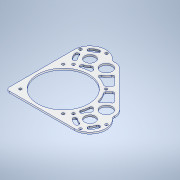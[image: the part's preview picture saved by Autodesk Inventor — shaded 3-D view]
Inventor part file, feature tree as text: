
AUTODESK INVENTOR PART (.ipt)
format: ipt  version: 2020 (Build 240168000, 168)  size: 512,512 bytes
history: native  units: in
note: dims shown in document units (in); Inventor stores cm internally (conversion verified against a paired STEP export)
features: extrude x4, sketch x3, fillet x1
ambient origin geometry x8: Origin, YZ Plane, XZ Plane, XY Plane, X Axis, Y Axis, Z Axis, Center Point
bodies: Solid1 (feature_tree)
feature tree (8):
  extrude  "Extrusion1"  Depth=4.5in
  extrude  "Extrusion2"  Depth=4.25in
  extrude  "Extrusion5"  Depth=0.25in
  fillet  "Fillet3"  Radius=5.9094in
  extrude  "Extrusion6"  Depth=0.25in
  sketch  "Sketch1"  dims[d0=3.8in d1=4.5in]
  sketch  "Sketch5"  dims[d2=0.196in d3=4.25in]
  sketch  "Sketch6"  dims[d6=0.125in d7=0.0in d8=6.5in d9=5.9094in d10=1.8in d11=0.6in d13=2.3622in d16=0.7874in d17=2.0in d18=0.875in d19=0.25in d20=0.0in d67=0.25in d68=0.0in d70=1.375in d71=0.25in d72=0.25in d73=0.25in d74=0.25in d76=0.125in d77=0.25in d78=0.25in d79=0.25in d82=0.25in d83=0.25in d100=0.0in d101=0.0in d102=0.25in d103=0.25in d104=0.25in d105=0.25in d110=0.25in d111=0.25in d112=0.25in d114=30.0deg]
